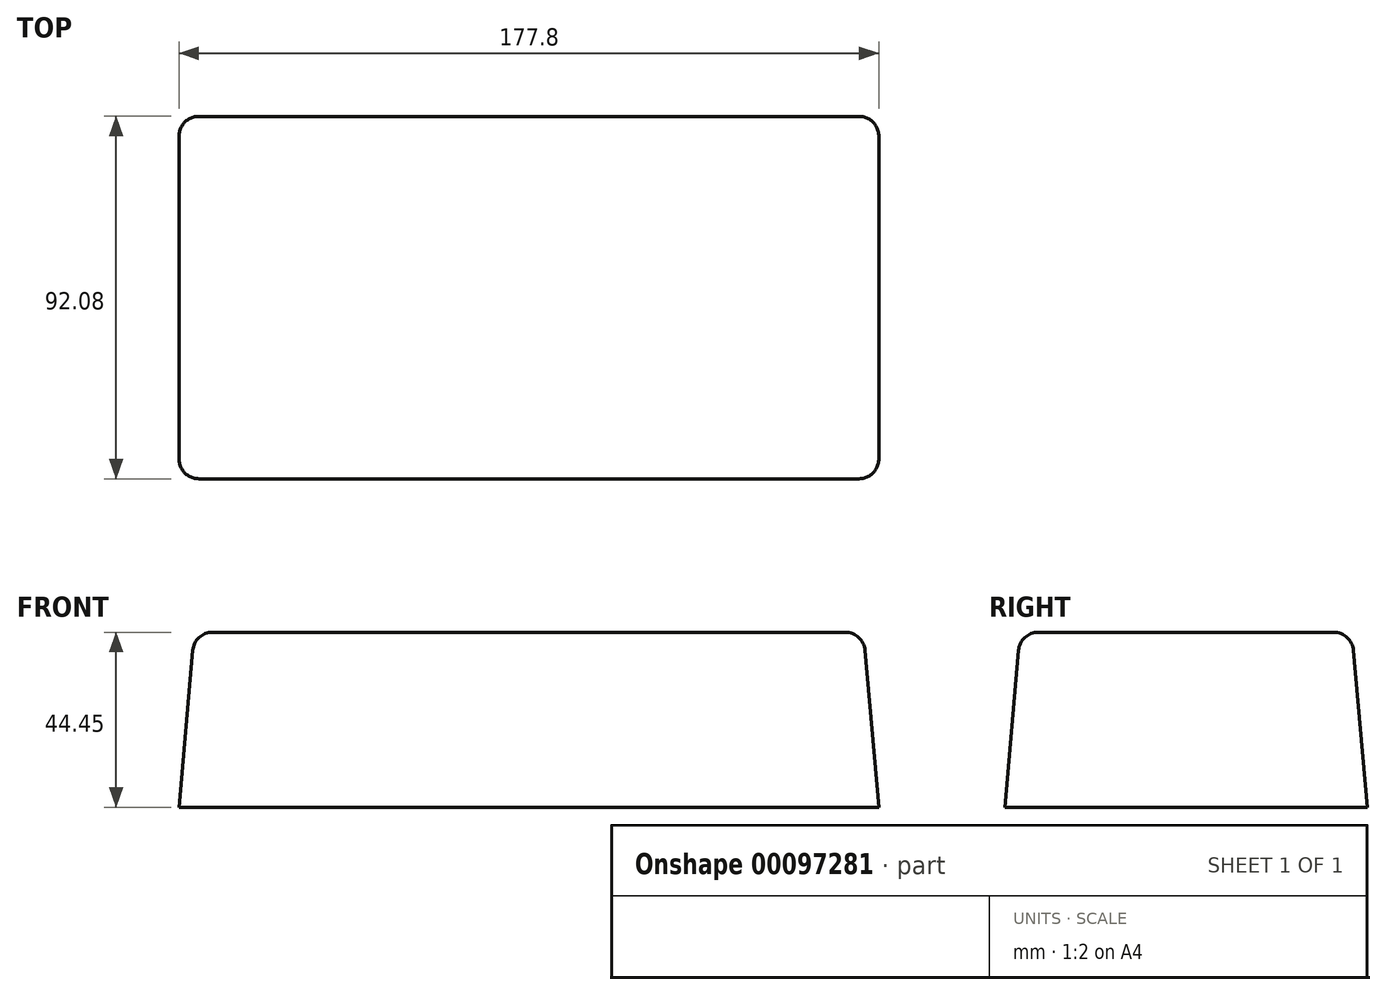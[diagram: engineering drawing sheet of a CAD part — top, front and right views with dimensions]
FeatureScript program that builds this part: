
annotation { "Feature Type Name" : "Feature", "Feature Type Description" : "" }
export const myFeature = defineFeature(function(context is Context, id is Id, definition is map)
    precondition{}
    {
        {
            var Q0;
            Q0=qCreatedBy(makeId("Top.planeOp"),FACE);
            var sketch = newSketch(context, id + "F0", { "sketchPlane" : qUnion([Q0])});
            skLineSegment(sketch, "E0.bottom", {"start": v(-88.9, -46.04) * mm, "end": v(88.9, -46.04) * mm});
            skLineSegment(sketch, "E0.top", {"start": v(-88.9, 46.04) * mm, "end": v(88.9, 46.04) * mm});
            skLineSegment(sketch, "E0.left", {"start": v(-88.9, -46.04) * mm, "end": v(-88.9, 46.04) * mm});
            skLineSegment(sketch, "E0.right", {"start": v(88.9, -46.04) * mm, "end": v(88.9, 46.04) * mm});
            skPoint(sketch, "E0.middle", {"position": v(0, 0) * mm});
            skSolve(sketch);
        }
        {
            var Q0;
            Q0=makeQuery(id+"F0.imprint","IMPRINT",FACE,{"disambiguationData":[TD([[makeQuery(id+"F0.imprint","IMPRINT",EDGE,{"derivedFrom":sQuery(id+"F0.wireOp",EDGE,"E0.bottom")}),1.0]])]});
            extrude(context, id + "F1", {"entities" : qUnion([Q0]), "depth" : 44.45 * mm, "hasDraft" : true, "draftAngle" : 5 * degree, "draftPullDirection" : true});
        }
        {
            var Q0;
            Q0=makeQuery(id+"F1.opExtrude","CAP_EDGE",EDGE,{"disambiguationData":[OSD([sQuery(id+"F0.wireOp",EDGE,"E0.bottom")])],"isStart":false});
            var Q1;
            Q1=makeQuery(id+"F1.opExtrude","SWEPT_EDGE",EDGE,{"disambiguationData":[OSD([sQuery(id+"F0.wireOp",EDGE,"E0.bottom"),sQuery(id+"F0.wireOp",EDGE,"E0.left")])]});
            var Q2;
            Q2=makeQuery(id+"F1.opExtrude","SWEPT_EDGE",EDGE,{"disambiguationData":[OSD([sQuery(id+"F0.wireOp",EDGE,"E0.bottom"),sQuery(id+"F0.wireOp",EDGE,"E0.right")])]});
            var Q3;
            Q3=makeQuery(id+"F1.opExtrude","CAP_EDGE",EDGE,{"disambiguationData":[OSD([sQuery(id+"F0.wireOp",EDGE,"E0.right")])],"isStart":false});
            var Q4;
            Q4=makeQuery(id+"F1.opExtrude","CAP_EDGE",EDGE,{"disambiguationData":[OSD([sQuery(id+"F0.wireOp",EDGE,"E0.left")])],"isStart":false});
            var Q5;
            Q5=makeQuery(id+"F1.opExtrude","CAP_EDGE",EDGE,{"disambiguationData":[OSD([sQuery(id+"F0.wireOp",EDGE,"E0.top")])],"isStart":false});
            var Q6;
            Q6=makeQuery(id+"F1.opExtrude","SWEPT_EDGE",EDGE,{"disambiguationData":[OSD([sQuery(id+"F0.wireOp",EDGE,"E0.top"),sQuery(id+"F0.wireOp",EDGE,"E0.left")])]});
            var Q7;
            Q7=makeQuery(id+"F1.opExtrude","SWEPT_EDGE",EDGE,{"disambiguationData":[OSD([sQuery(id+"F0.wireOp",EDGE,"E0.top"),sQuery(id+"F0.wireOp",EDGE,"E0.right")])]});
            fillet(context, id + "F2", {"entities" : qUnion([Q0, Q1, Q2, Q3, Q4, Q5, Q6, Q7]), "radius" : 5.08 * mm, "tangentPropagation" : true, "allowEdgeOverflow" : false});
        }
    });
